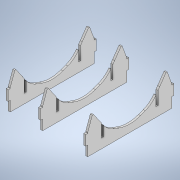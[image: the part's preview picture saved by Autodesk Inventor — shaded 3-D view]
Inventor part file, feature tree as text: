
AUTODESK INVENTOR PART (.ipt)
format: ipt  version: 2020 (Build 240168000, 168)  size: 266,240 bytes
history: native  units: mm
features: other x5, sketch x4, extrude x3, mirror x1, reference x1
ambient origin geometry x8: Origin, YZ Plane, XZ Plane, XY Plane, X Axis, Y Axis, Z Axis, Center Point
bodies: Body1 (feature_tree)
feature tree (14):
  other  "Твердое тело1"
  extrude  "Выдавливание1"  Depth=332.0mm
  sketch  "Эскиз2"
  other  "РабПлоскость1"
  extrude  "Выдавливание4"  Depth=170.0mm
  extrude  "Выдавливание5"  Depth=166.0mm TaperAngle=0.0deg
  mirror  "Зеркальное отражение2"
  sketch  "Эскиз1"
  sketch  "Эскиз4"
  sketch  "Эскиз5"
  reference  "Ссылка1"
  parser-record x1  (decoder bookkeeping rows leaked as tree rows — omitted from the tree; the rows remain in map.json)
  other  "Main_agan.iam"
  other  "44260_txm torquenado dc motor:1"
note: 1 file-system path scrubbed to <path> (originals preserved in map.json)
